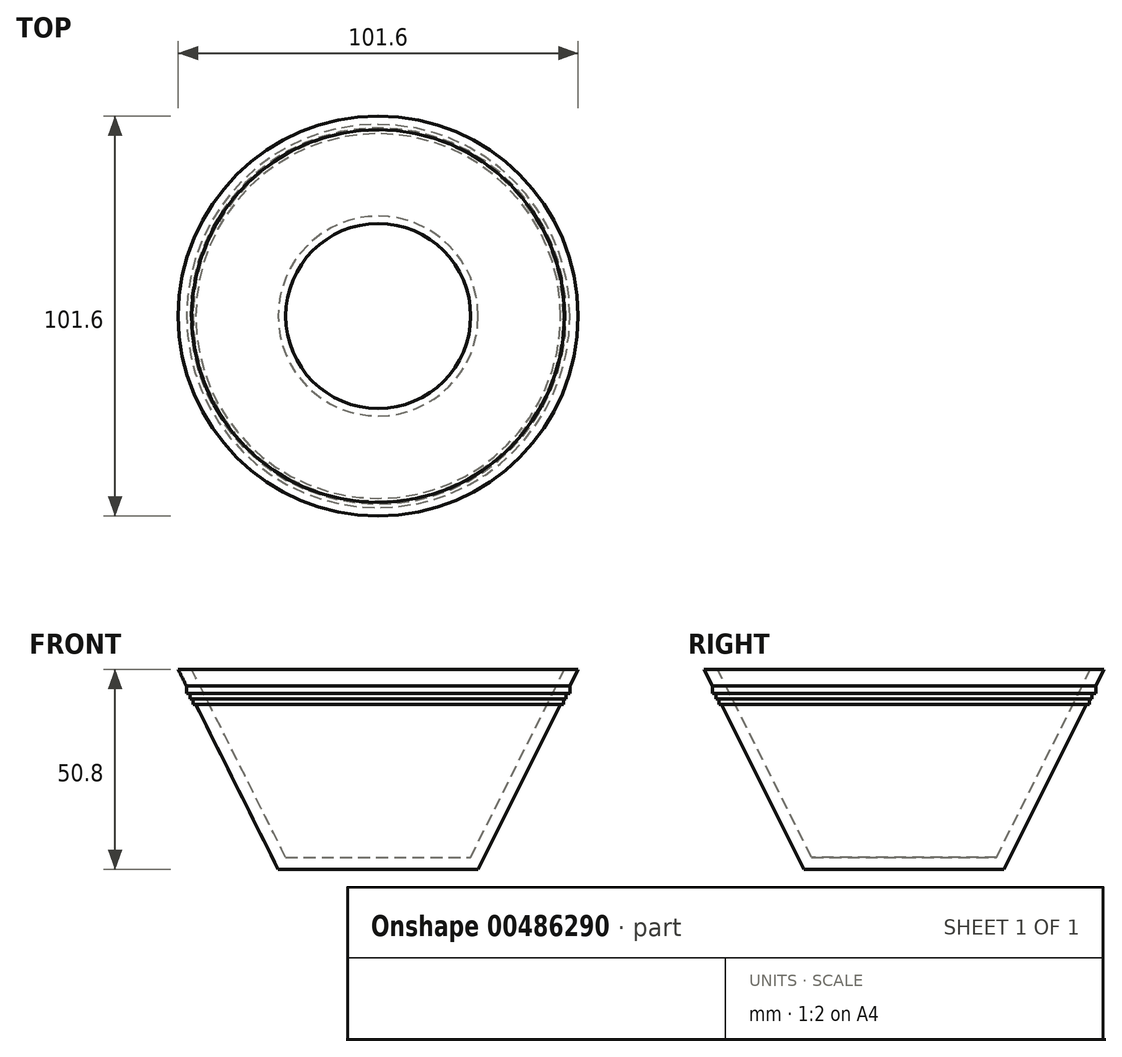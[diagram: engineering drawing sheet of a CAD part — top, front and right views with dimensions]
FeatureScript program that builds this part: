
annotation { "Feature Type Name" : "Feature", "Feature Type Description" : "" }
export const myFeature = defineFeature(function(context is Context, id is Id, definition is map)
    precondition{}
    {
        {
            var Q0;
            Q0=qCreatedBy(makeId("Right.planeOp"),FACE);
            var sketch = newSketch(context, id + "F0", { "sketchPlane" : qUnion([Q0])});
            skLineSegment(sketch, "E0", {"start": v(0, 0) * mm, "end": v(25.4, 0) * mm});
            skLineSegment(sketch, "E1", {"start": v(25.4, 0) * mm, "end": v(50.8, 50.8) * mm});
            skLineSegment(sketch, "E2", {"start": v(0, 0) * mm, "end": v(0, 50.8) * mm, "construction": true});
            skLineSegment(sketch, "E3.0", {"start": v(23.5, 3.07) * mm, "end": v(47.36, 50.8) * mm});
            skLineSegment(sketch, "E3.1", {"start": v(0, 3.07) * mm, "end": v(23.5, 3.07) * mm});
            skLineSegment(sketch, "E4", {"start": v(0, 3.07) * mm, "end": v(0, 0) * mm});
            skLineSegment(sketch, "E5", {"start": v(50.8, 50.8) * mm, "end": v(47.36, 50.8) * mm});
            skLineSegment(sketch, "E6", {"start": v(48.69, 46.58) * mm, "end": v(48.69, 44.76) * mm});
            skLineSegment(sketch, "E7", {"start": v(48.69, 44.76) * mm, "end": v(47.78, 44.76) * mm});
            skLineSegment(sketch, "E8", {"start": v(47.78, 44.76) * mm, "end": v(47.78, 43.28) * mm});
            skLineSegment(sketch, "E9", {"start": v(47.78, 43.28) * mm, "end": v(47.04, 43.28) * mm});
            skLineSegment(sketch, "E10", {"start": v(47.04, 43.28) * mm, "end": v(47.04, 41.87) * mm});
            skLineSegment(sketch, "E11", {"start": v(47.04, 41.87) * mm, "end": v(46.34, 41.87) * mm});
            skPoint(sketch, "E12.visualSharp", {"position": v(47.04, 41.87) * mm});
            skPoint(sketch, "E13.visualSharp", {"position": v(47.78, 43.28) * mm});
            skSolve(sketch);
        }
        {
            var Q0;
            Q0 = qSketchRegion(id + "F0", true);
            var Q1;
            Q1=sQuery(id+"F0.wireOp",EDGE,"E2");
            revolve(context, id + "F1", {"entities" : qUnion([Q0]), "axis" : qUnion([Q1]), "revolveType" : RevolveType.FULL});
        }
    });
